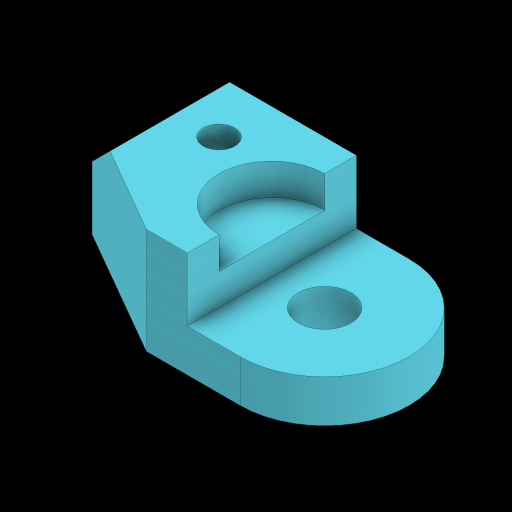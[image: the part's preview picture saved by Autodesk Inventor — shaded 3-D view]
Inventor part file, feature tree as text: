
AUTODESK INVENTOR PART (.ipt)
format: ipt  version: 2024 (Build 280153000, 153)  size: 162,304 bytes
history: native  units: in
note: dims shown in document units (in); Inventor stores cm internally (conversion verified against a paired STEP export)
features: extrude x3, sketch x3, chamfer x1
ambient origin geometry x8: Origin, YZ Plane, XZ Plane, XY Plane, X Axis, Y Axis, Z Axis, Center Point
bodies: Solid1 (feature_tree)
feature tree (7):
  extrude  "MAIN BLOCK"  Depth=5.25in
  extrude  "SQUARE CUTOUT"  Depth=2.25in
  extrude  "HALF CIRCLE CUTOUT"  Depth=0.75in
  chamfer  "REAR CHAMFER"  Distance=1.25in
  sketch  "Sketch1"  dims[d0=4.0in d1=5.25in]
  sketch  "Sketch2"  dims[d4=60.0deg d5=2.25in]
  sketch  "Sketch3"  dims[d6=1.25in d7=0.75in d8=1.25in d9=3.25in d10=2.5in d11=0.0in d12=1.25in d13=1.5in d14=0.0in d15=2.5in d16=0.75in d17=0.0in d18=1.0in d19=0.125in d20=45.0deg]
